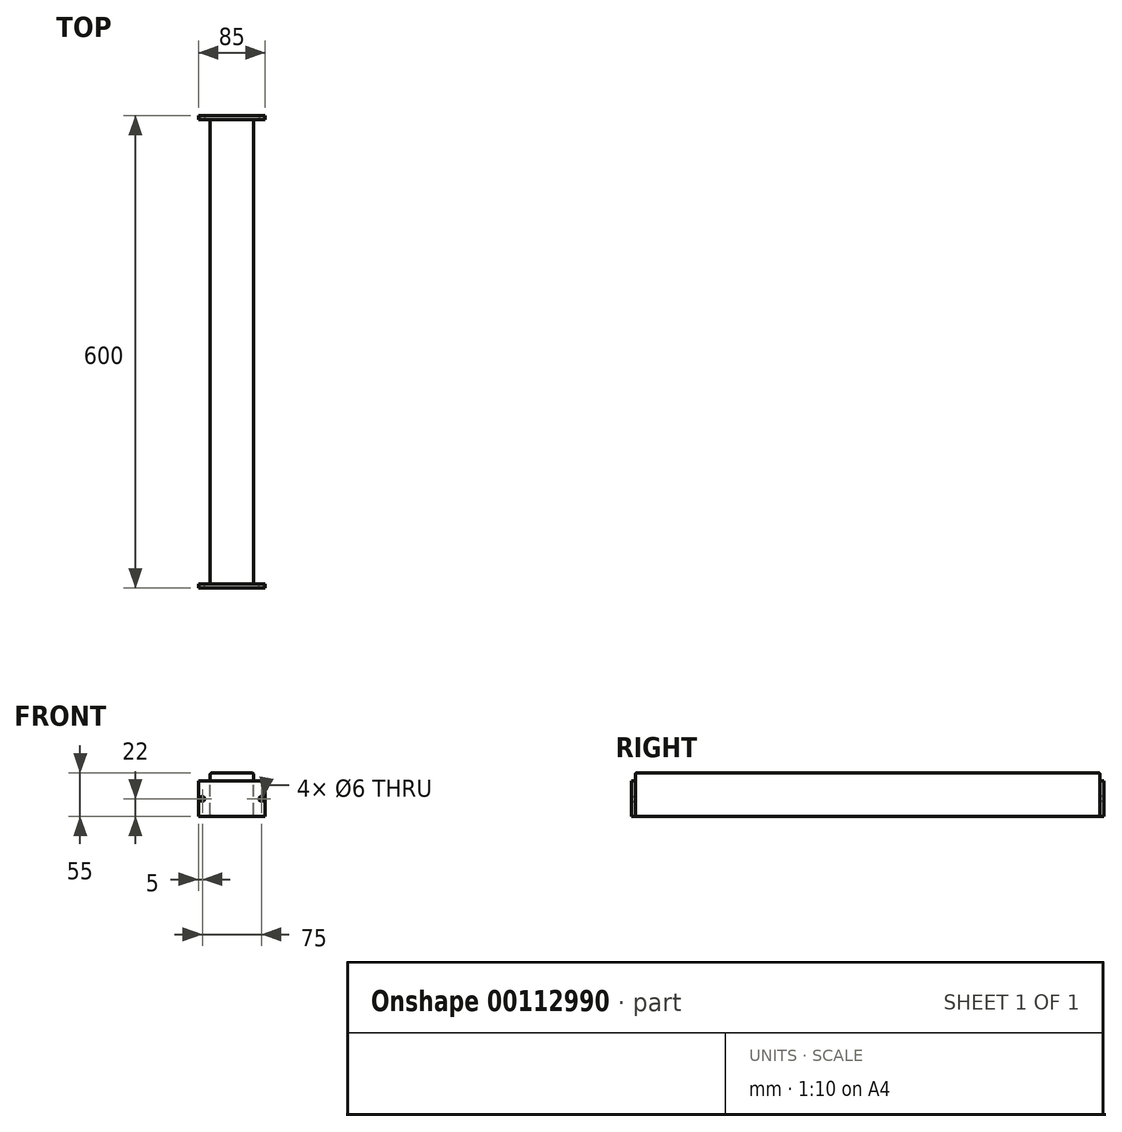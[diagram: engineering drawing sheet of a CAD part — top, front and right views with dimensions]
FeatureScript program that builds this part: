
annotation { "Feature Type Name" : "Feature", "Feature Type Description" : "" }
export const myFeature = defineFeature(function(context is Context, id is Id, definition is map)
    precondition{}
    {
        {
            var Q0;
            Q0=qCreatedBy(makeId("Front.planeOp"),FACE);
            var sketch = newSketch(context, id + "F0", { "sketchPlane" : qUnion([Q0])});
            skLineSegment(sketch, "E0.bottom", {"start": v(27.5, 0) * mm, "end": v(-27.5, 0) * mm});
            skLineSegment(sketch, "E0.top", {"start": v(27.5, 55) * mm, "end": v(-27.5, 55) * mm});
            skLineSegment(sketch, "E0.left", {"start": v(27.5, 0) * mm, "end": v(27.5, 55) * mm});
            skLineSegment(sketch, "E0.right", {"start": v(-27.5, 0) * mm, "end": v(-27.5, 55) * mm});
            skPoint(sketch, "E0.middle", {"position": v(0, 27.5) * mm});
            skSolve(sketch);
        }
        {
            var Q0;
            Q0=makeQuery(id+"F0.imprint","IMPRINT",FACE,{"disambiguationData":[TD([[makeQuery(id+"F0.imprint","IMPRINT",EDGE,{"derivedFrom":sQuery(id+"F0.wireOp",EDGE,"E0.bottom")}),-1.0]])]});
            extrude(context, id + "F1", {"entities" : qUnion([Q0]), "depth" : 590 * mm});
        }
        {
            var Q0;
            Q0=makeQuery(id+"F1.opExtrude","CAP_FACE",FACE,{"disambiguationData":[OSD([sQuery(id+"F0.wireOp",EDGE,"E0.bottom"),sQuery(id+"F0.wireOp",EDGE,"E0.top"),sQuery(id+"F0.wireOp",EDGE,"E0.left"),sQuery(id+"F0.wireOp",EDGE,"E0.right")])],"isStart":true});
            var sketch = newSketch(context, id + "F2", { "sketchPlane" : qUnion([Q0])});
            skLineSegment(sketch, "E1.bottom", {"start": v(42.5, 0) * mm, "end": v(-42.5, 0) * mm});
            skLineSegment(sketch, "E1.top", {"start": v(42.5, 45) * mm, "end": v(-42.5, 45) * mm});
            skLineSegment(sketch, "E1.left", {"start": v(42.5, 0) * mm, "end": v(42.5, 45) * mm});
            skLineSegment(sketch, "E1.right", {"start": v(-42.5, 0) * mm, "end": v(-42.5, 45) * mm});
            skCircle(sketch, "E2", {"center": v(-37.5, 22) * mm, "radius": 3 * mm});
            skCircle(sketch, "E3", {"center": v(37.5, 22) * mm, "radius": 3 * mm});
            skSolve(sketch);
        }
        {
            var Q0;
            {var subQ0=sQuery(id+"F2.wireOp",EDGE,"E1.right");Q0=makeQuery(id+"F2.imprint","IMPRINT",FACE,{"disambiguationData":[TD([[makeQuery(id+"F2.imprint","IMPRINT",EDGE,{"derivedFrom":subQ0}),-1.0]])]});}
            var Q1;
            {var subQ0=sQuery(id+"F2.wireOp",EDGE,"E1.bottom");var subQ1=makeQuery(id+"F1.opExtrude","CAP_EDGE",EDGE,{"disambiguationData":[OSD([sQuery(id+"F0.wireOp",EDGE,"E0.left")])],"isStart":true});var subQ2=makeQuery(id+"F2.imprint","INTERSECT",VERTEX,{"derivedFrom":[subQ1,subQ0]});var subQ3=makeQuery(id+"F1.opExtrude","CAP_EDGE",EDGE,{"disambiguationData":[OSD([sQuery(id+"F0.wireOp",EDGE,"E0.right")])],"isStart":true});var subQ4=makeQuery(id+"F2.imprint","INTERSECT",VERTEX,{"derivedFrom":[subQ3,subQ0]});Q1=makeQuery(id+"F2.imprint","IMPRINT",FACE,{"disambiguationData":[TD([[makeQuery(id+"F2.imprint","IMPRINT",EDGE,{"disambiguationData":[TD([[subQ2,-1.0],[subQ4,1.0]])],"derivedFrom":subQ0}),1.0]])]});}
            var Q2;
            {var subQ0=sQuery(id+"F2.wireOp",EDGE,"E1.left");Q2=makeQuery(id+"F2.imprint","IMPRINT",FACE,{"disambiguationData":[TD([[makeQuery(id+"F2.imprint","IMPRINT",EDGE,{"derivedFrom":subQ0}),1.0]])]});}
            extrude(context, id + "F3", {"entities" : qUnion([Q0, Q1, Q2]), "operationType" : NewBodyOperationType.ADD, "depth" : 5 * mm});
        }
        {
            var Q0;
            Q0=makeQuery(id+"F1.opExtrude","CAP_FACE",FACE,{"disambiguationData":[OSD([sQuery(id+"F0.wireOp",EDGE,"E0.bottom"),sQuery(id+"F0.wireOp",EDGE,"E0.top"),sQuery(id+"F0.wireOp",EDGE,"E0.left"),sQuery(id+"F0.wireOp",EDGE,"E0.right")])],"isStart":false});
            var sketch = newSketch(context, id + "F4", { "sketchPlane" : qUnion([Q0])});
            skLineSegment(sketch, "E4.bottom", {"start": v(42.5, 0) * mm, "end": v(-42.5, 0) * mm});
            skLineSegment(sketch, "E4.top", {"start": v(42.5, 45) * mm, "end": v(-42.5, 45) * mm});
            skLineSegment(sketch, "E4.left", {"start": v(42.5, 0) * mm, "end": v(42.5, 45) * mm});
            skLineSegment(sketch, "E4.right", {"start": v(-42.5, 0) * mm, "end": v(-42.5, 45) * mm});
            skCircle(sketch, "E5", {"center": v(-37.5, 22) * mm, "radius": 3 * mm});
            skCircle(sketch, "E6", {"center": v(37.5, 22) * mm, "radius": 3 * mm});
            skSolve(sketch);
        }
        {
            var Q0;
            {var subQ0=sQuery(id+"F4.wireOp",EDGE,"E4.right");Q0=makeQuery(id+"F4.imprint","IMPRINT",FACE,{"disambiguationData":[TD([[makeQuery(id+"F4.imprint","IMPRINT",EDGE,{"derivedFrom":subQ0}),-1.0]])]});}
            var Q1;
            {var subQ0=sQuery(id+"F4.wireOp",EDGE,"E4.bottom");var subQ1=makeQuery(id+"F1.opExtrude","CAP_EDGE",EDGE,{"disambiguationData":[OSD([sQuery(id+"F0.wireOp",EDGE,"E0.left")])],"isStart":false});var subQ2=makeQuery(id+"F4.imprint","INTERSECT",VERTEX,{"derivedFrom":[subQ1,subQ0]});Q1=makeQuery(id+"F4.imprint","IMPRINT",FACE,{"disambiguationData":[TD([[makeQuery(id+"F4.imprint","IMPRINT",EDGE,{"disambiguationData":[TD([[subQ2,-1.0]])],"derivedFrom":subQ0}),-1.0]])]});}
            var Q2;
            {var subQ5=sQuery(id+"F4.wireOp",EDGE,"E4.left");Q2=makeQuery(id+"F4.imprint","IMPRINT",FACE,{"disambiguationData":[TD([[makeQuery(id+"F4.imprint","IMPRINT",EDGE,{"derivedFrom":subQ5}),1.0]])]});}
            extrude(context, id + "F5", {"entities" : qUnion([Q0, Q1, Q2]), "operationType" : NewBodyOperationType.ADD, "depth" : 5 * mm});
        }
        {
            var Q0;
            Q0=makeQuery(id+"F1.opExtrude","SWEPT_FACE",FACE,{"disambiguationData":[OSD([sQuery(id+"F0.wireOp",EDGE,"E0.top")])]});
            var Q1;
            Q1=makeQuery(id+"F1.opExtrude","SWEPT_EDGE",EDGE,{"disambiguationData":[OSD([sQuery(id+"F0.wireOp",EDGE,"E0.bottom"),sQuery(id+"F0.wireOp",EDGE,"E0.right")])]});
            var Q2;
            Q2=makeQuery(id+"F1.opExtrude","SWEPT_EDGE",EDGE,{"disambiguationData":[OSD([sQuery(id+"F0.wireOp",EDGE,"E0.bottom"),sQuery(id+"F0.wireOp",EDGE,"E0.left")])]});
            fillet(context, id + "F6", {"entities" : qUnion([Q0, Q1, Q2]), "radius" : 2 * mm, "tangentPropagation" : true, "allowEdgeOverflow" : false});
        }
    });
